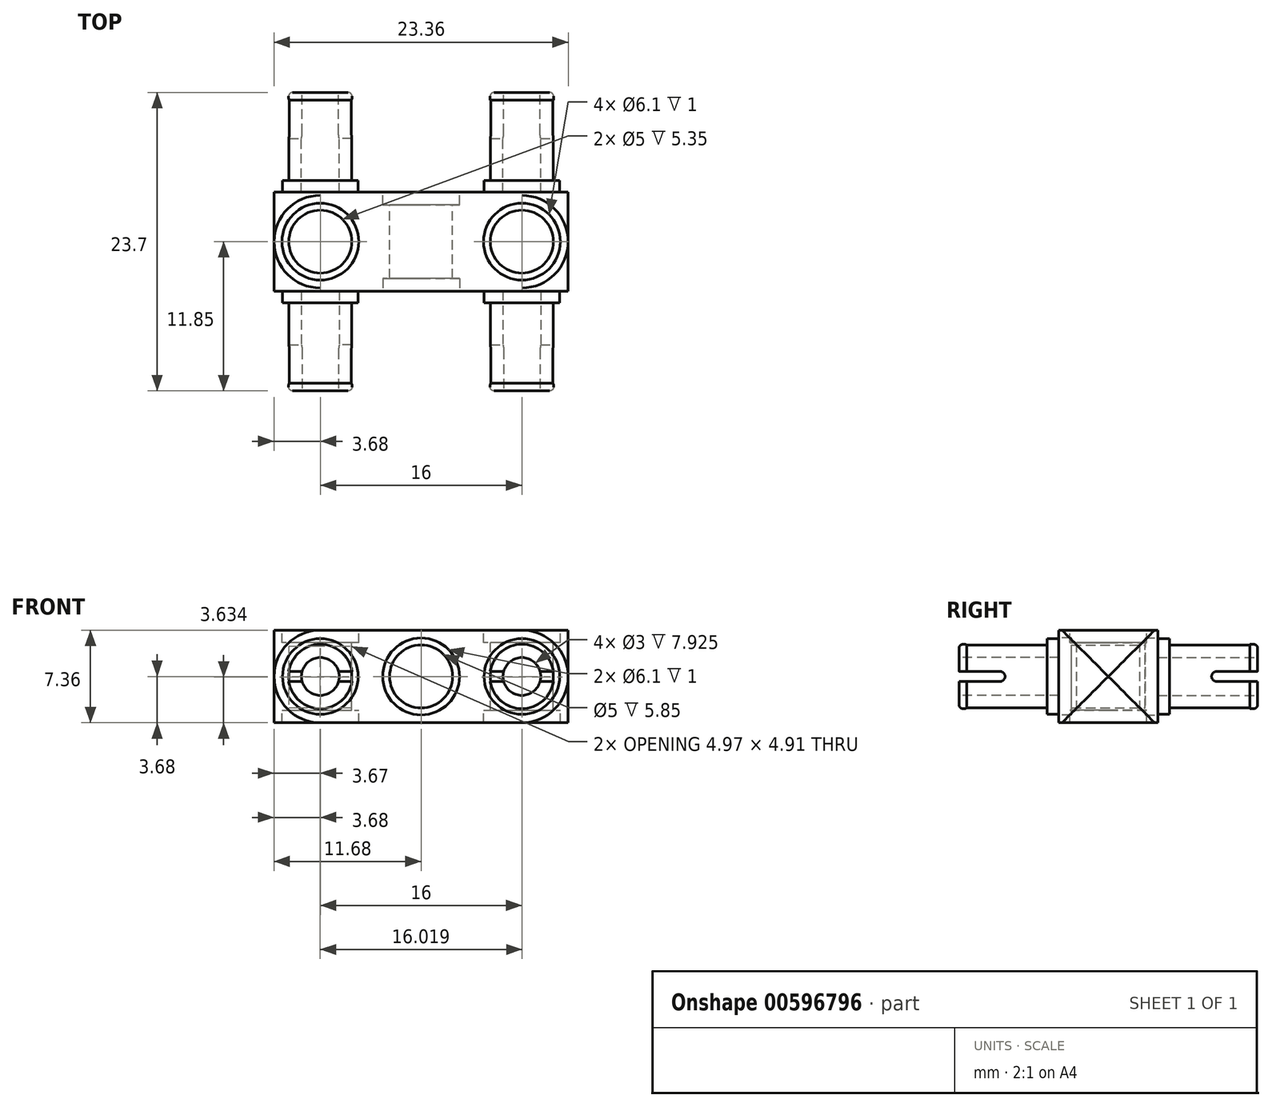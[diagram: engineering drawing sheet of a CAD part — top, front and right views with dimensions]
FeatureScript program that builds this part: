
annotation { "Feature Type Name" : "Feature", "Feature Type Description" : "" }
export const myFeature = defineFeature(function(context is Context, id is Id, definition is map)
    precondition{}
    {
        {
            var Q0;
            Q0=qCreatedBy(makeId("Front.planeOp"),FACE);
            var sketch = newSketch(context, id + "F0", { "sketchPlane" : qUnion([Q0])});
            skLineSegment(sketch, "E0.bottom", {"start": v(11.68, 3.67) * mm, "end": v(-11.68, 3.67) * mm});
            skLineSegment(sketch, "E0.top", {"start": v(11.68, -3.67) * mm, "end": v(-11.68, -3.67) * mm});
            skLineSegment(sketch, "E0.left", {"start": v(11.68, 3.67) * mm, "end": v(11.68, -3.67) * mm});
            skLineSegment(sketch, "E0.right", {"start": v(-11.68, 3.67) * mm, "end": v(-11.68, -3.67) * mm});
            skPoint(sketch, "E0.middle", {"position": v(0, 0) * mm});
            skCircle(sketch, "E1", {"center": v(-8, 0) * mm, "radius": 3.67 * mm});
            skCircle(sketch, "E2", {"center": v(8, 0) * mm, "radius": 3.67 * mm});
            skCircle(sketch, "E3", {"center": v(0, 0) * mm, "radius": 2.5 * mm});
            skCircle(sketch, "E4", {"center": v(0, 0) * mm, "radius": 3.05 * mm});
            skCircle(sketch, "E5", {"center": v(-8, 0) * mm, "radius": 3 * mm});
            skCircle(sketch, "E6", {"center": v(8, 0) * mm, "radius": 3 * mm});
            skCircle(sketch, "E7", {"center": v(-8, 0) * mm, "radius": 2.5 * mm});
            skCircle(sketch, "E8", {"center": v(8, 0) * mm, "radius": 2.5 * mm});
            skSolve(sketch);
        }
        {
            var Q0;
            Q0=makeQuery(id+"F0.imprint","IMPRINT",FACE,{"disambiguationData":[TD([[makeQuery(id+"F0.imprint","IMPRINT",EDGE,{"derivedFrom":sQuery(id+"F0.wireOp",EDGE,"E4")}),-1.0]])]});
            var Q1;
            {var subQ0=sQuery(id+"F0.wireOp",EDGE,"E1");var subQ1=makeQuery(id+"F0.imprint","INTERSECT",VERTEX,{"derivedFrom":[sQuery(id+"F0.wireOp",EDGE,"E0.bottom"),subQ0]});Q1=makeQuery(id+"F0.imprint","IMPRINT",FACE,{"disambiguationData":[TD([[makeQuery(id+"F0.imprint","IMPRINT",EDGE,{"disambiguationData":[TD([[subQ1,-1.0]])],"derivedFrom":subQ0}),1.0]])]});}
            var Q2;
            {var subQ0=sQuery(id+"F0.wireOp",EDGE,"E2");var subQ1=makeQuery(id+"F0.imprint","INTERSECT",VERTEX,{"derivedFrom":[sQuery(id+"F0.wireOp",EDGE,"E0.bottom"),subQ0]});Q2=makeQuery(id+"F0.imprint","IMPRINT",FACE,{"disambiguationData":[TD([[makeQuery(id+"F0.imprint","IMPRINT",EDGE,{"disambiguationData":[TD([[subQ1,1.0]])],"derivedFrom":subQ0}),1.0]])]});}
            var Q3;
            Q3=makeQuery(id+"F0.imprint","IMPRINT",FACE,{"disambiguationData":[TD([[makeQuery(id+"F0.imprint","IMPRINT",EDGE,{"derivedFrom":sQuery(id+"F0.wireOp",EDGE,"E3")}),-1.0]])]});
            extrude(context, id + "F1", {"entities" : qUnion([Q0, Q1, Q2, Q3]), "endBound" : BoundingType.SYMMETRIC, "depth" : 7.85 * mm, "offsetDistance" : 25 * mm});
        }
        {
            var Q0;
            Q0=makeQuery(id+"F0.imprint","IMPRINT",FACE,{"disambiguationData":[TD([[makeQuery(id+"F0.imprint","IMPRINT",EDGE,{"derivedFrom":sQuery(id+"F0.wireOp",EDGE,"E5")}),1.0]])]});
            var Q1;
            Q1=makeQuery(id+"F0.imprint","IMPRINT",FACE,{"disambiguationData":[TD([[makeQuery(id+"F0.imprint","IMPRINT",EDGE,{"derivedFrom":sQuery(id+"F0.wireOp",EDGE,"E6")}),1.0]])]});
            extrude(context, id + "F2", {"entities" : qUnion([Q0, Q1]), "operationType" : NewBodyOperationType.ADD, "endBound" : BoundingType.SYMMETRIC, "depth" : 9.7 * mm, "offsetDistance" : 25 * mm});
        }
        {
            var Q0;
            Q0=makeQuery(id+"F0.imprint","IMPRINT",FACE,{"disambiguationData":[TD([[makeQuery(id+"F0.imprint","IMPRINT",EDGE,{"derivedFrom":sQuery(id+"F0.wireOp",EDGE,"E7")}),1.0]])]});
            var Q1;
            Q1=makeQuery(id+"F0.imprint","IMPRINT",FACE,{"disambiguationData":[TD([[makeQuery(id+"F0.imprint","IMPRINT",EDGE,{"derivedFrom":sQuery(id+"F0.wireOp",EDGE,"E8")}),1.0]])]});
            extrude(context, id + "F3", {"entities" : qUnion([Q0, Q1]), "operationType" : NewBodyOperationType.ADD, "endBound" : BoundingType.SYMMETRIC, "depth" : 22.5 * mm, "offsetDistance" : 25 * mm});
        }
        {
            var Q0;
            Q0=makeQuery(id+"F3.opExtrude","CAP_FACE",FACE,{"disambiguationData":[OSD([sQuery(id+"F0.wireOp",EDGE,"E7")])],"isStart":false});
            var sketch = newSketch(context, id + "F4", { "sketchPlane" : qUnion([Q0])});
            skCircle(sketch, "E9", {"center": v(-8, 0) * mm, "radius": 2.55 * mm});
            skSolve(sketch);
        }
        {
            var Q0;
            Q0=qSketchRegion(id+"F4",true);
            extrude(context, id + "F5", {"entities" : qUnion([Q0]), "operationType" : NewBodyOperationType.ADD, "depth" : 0.6 * mm, "offsetDistance" : 25 * mm});
        }
        {
            var Q0;
            Q0=makeQuery(id+"F3.opExtrude","CAP_FACE",FACE,{"disambiguationData":[OSD([sQuery(id+"F0.wireOp",EDGE,"E8")])],"isStart":false});
            var sketch = newSketch(context, id + "F6", { "sketchPlane" : qUnion([Q0])});
            skCircle(sketch, "E10", {"center": v(8, 0) * mm, "radius": 2.55 * mm});
            skSolve(sketch);
        }
        {
            var Q0;
            Q0=qSketchRegion(id+"F6",true);
            extrude(context, id + "F7", {"entities" : qUnion([Q0]), "operationType" : NewBodyOperationType.ADD, "depth" : 0.6 * mm, "offsetDistance" : 25 * mm});
        }
        {
            var Q0;
            Q0=makeQuery(id+"F3.opExtrude","CAP_FACE",FACE,{"disambiguationData":[OSD([sQuery(id+"F0.wireOp",EDGE,"E7")])],"isStart":true});
            var sketch = newSketch(context, id + "F8", { "sketchPlane" : qUnion([Q0])});
            skCircle(sketch, "E11", {"center": v(8, 0) * mm, "radius": 2.55 * mm});
            skSolve(sketch);
        }
        {
            var Q0;
            Q0=qSketchRegion(id+"F8",true);
            extrude(context, id + "F9", {"entities" : qUnion([Q0]), "operationType" : NewBodyOperationType.ADD, "depth" : 0.6 * mm, "offsetDistance" : 25 * mm});
        }
        {
            var Q0;
            Q0=makeQuery(id+"F3.opExtrude","CAP_FACE",FACE,{"disambiguationData":[OSD([sQuery(id+"F0.wireOp",EDGE,"E8")])],"isStart":true});
            var sketch = newSketch(context, id + "F10", { "sketchPlane" : qUnion([Q0])});
            skCircle(sketch, "E12", {"center": v(-8, 0) * mm, "radius": 2.55 * mm});
            skSolve(sketch);
        }
        {
            var Q0;
            Q0=qSketchRegion(id+"F10",true);
            extrude(context, id + "F11", {"entities" : qUnion([Q0]), "operationType" : NewBodyOperationType.ADD, "depth" : 0.6 * mm, "offsetDistance" : 25 * mm});
        }
        {
            var Q0;
            Q0=makeQuery(id+"F9.opExtrude","CAP_FACE",FACE,{"disambiguationData":[OSD([sQuery(id+"F8.wireOp",EDGE,"E11")])],"isStart":false});
            var sketch = newSketch(context, id + "F12", { "sketchPlane" : qUnion([Q0])});
            skCircle(sketch, "E13", {"center": v(8, 0) * mm, "radius": 1.5 * mm});
            skSolve(sketch);
        }
        {
            var Q0;
            Q0=qSketchRegion(id+"F12",true);
            var Q1;
            Q1=makeQuery(id+"F1.opExtrude","CAP_FACE",FACE,{"disambiguationData":[OSD([sQuery(id+"F0.wireOp",EDGE,"E0.bottom"),sQuery(id+"F0.wireOp",EDGE,"E0.top"),sQuery(id+"F0.wireOp",EDGE,"E1"),sQuery(id+"F0.wireOp",EDGE,"E2"),sQuery(id+"F0.wireOp",EDGE,"E3"),sQuery(id+"F0.wireOp",EDGE,"E5"),sQuery(id+"F0.wireOp",EDGE,"E6")])],"isStart":true});
            extrude(context, id + "F13", {"entities" : qUnion([Q0]), "operationType" : NewBodyOperationType.REMOVE, "endBound" : BoundingType.UP_TO_SURFACE, "oppositeDirection" : true, "depth" : 25 * mm, "endBoundEntityFace" : qUnion([Q1]), "offsetDistance" : 25 * mm});
        }
        {
            var Q0;
            Q0=makeQuery(id+"F11.opExtrude","CAP_FACE",FACE,{"disambiguationData":[OSD([sQuery(id+"F10.wireOp",EDGE,"E12")])],"isStart":false});
            var sketch = newSketch(context, id + "F14", { "sketchPlane" : qUnion([Q0])});
            skCircle(sketch, "E14", {"center": v(-8, 0) * mm, "radius": 1.5 * mm});
            skSolve(sketch);
        }
        {
            var Q0;
            Q0=qSketchRegion(id+"F14",true);
            var Q1;
            Q1=makeQuery(id+"F1.opExtrude","CAP_FACE",FACE,{"disambiguationData":[OSD([sQuery(id+"F0.wireOp",EDGE,"E0.bottom"),sQuery(id+"F0.wireOp",EDGE,"E0.top"),sQuery(id+"F0.wireOp",EDGE,"E1"),sQuery(id+"F0.wireOp",EDGE,"E2"),sQuery(id+"F0.wireOp",EDGE,"E3"),sQuery(id+"F0.wireOp",EDGE,"E5"),sQuery(id+"F0.wireOp",EDGE,"E6")])],"isStart":true});
            extrude(context, id + "F15", {"entities" : qUnion([Q0]), "operationType" : NewBodyOperationType.REMOVE, "endBound" : BoundingType.UP_TO_SURFACE, "oppositeDirection" : true, "depth" : 25 * mm, "endBoundEntityFace" : qUnion([Q1]), "offsetDistance" : 25 * mm});
        }
        {
            var Q0;
            Q0=makeQuery(id+"F7.opExtrude","CAP_FACE",FACE,{"disambiguationData":[OSD([sQuery(id+"F6.wireOp",EDGE,"E10")])],"isStart":false});
            var sketch = newSketch(context, id + "F16", { "sketchPlane" : qUnion([Q0])});
            skCircle(sketch, "E15", {"center": v(8, 0) * mm, "radius": 1.5 * mm});
            skSolve(sketch);
        }
        {
            var Q0;
            Q0=qSketchRegion(id+"F16",true);
            var Q1;
            Q1=makeQuery(id+"F1.opExtrude","CAP_FACE",FACE,{"disambiguationData":[OSD([sQuery(id+"F0.wireOp",EDGE,"E0.bottom"),sQuery(id+"F0.wireOp",EDGE,"E0.top"),sQuery(id+"F0.wireOp",EDGE,"E1"),sQuery(id+"F0.wireOp",EDGE,"E2"),sQuery(id+"F0.wireOp",EDGE,"E3"),sQuery(id+"F0.wireOp",EDGE,"E5"),sQuery(id+"F0.wireOp",EDGE,"E6")])],"isStart":false});
            extrude(context, id + "F17", {"entities" : qUnion([Q0]), "operationType" : NewBodyOperationType.REMOVE, "endBound" : BoundingType.UP_TO_SURFACE, "oppositeDirection" : true, "depth" : 25 * mm, "endBoundEntityFace" : qUnion([Q1]), "offsetDistance" : 25 * mm});
        }
        {
            var Q0;
            Q0=makeQuery(id+"F5.opExtrude","CAP_FACE",FACE,{"disambiguationData":[OSD([sQuery(id+"F4.wireOp",EDGE,"E9")])],"isStart":false});
            var sketch = newSketch(context, id + "F18", { "sketchPlane" : qUnion([Q0])});
            skCircle(sketch, "E16", {"center": v(-8, 0) * mm, "radius": 1.5 * mm});
            skSolve(sketch);
        }
        {
            var Q0;
            Q0=qSketchRegion(id+"F18",true);
            var Q1;
            Q1=makeQuery(id+"F1.opExtrude","CAP_FACE",FACE,{"disambiguationData":[OSD([sQuery(id+"F0.wireOp",EDGE,"E0.bottom"),sQuery(id+"F0.wireOp",EDGE,"E0.top"),sQuery(id+"F0.wireOp",EDGE,"E1"),sQuery(id+"F0.wireOp",EDGE,"E2"),sQuery(id+"F0.wireOp",EDGE,"E3"),sQuery(id+"F0.wireOp",EDGE,"E5"),sQuery(id+"F0.wireOp",EDGE,"E6")])],"isStart":false});
            extrude(context, id + "F19", {"entities" : qUnion([Q0]), "operationType" : NewBodyOperationType.REMOVE, "endBound" : BoundingType.UP_TO_SURFACE, "oppositeDirection" : true, "depth" : 25 * mm, "endBoundEntityFace" : qUnion([Q1]), "offsetDistance" : 25 * mm});
        }
        {
            var Q0;
            Q0=makeQuery(id+"F5.opExtrude","CAP_EDGE",EDGE,{"disambiguationData":[OSD([sQuery(id+"F4.wireOp",EDGE,"E9")])],"isStart":false});
            var Q1;
            Q1=makeQuery(id+"F5.opExtrude","CAP_EDGE",EDGE,{"disambiguationData":[OSD([sQuery(id+"F4.wireOp",EDGE,"E9")])],"isStart":true});
            var Q2;
            Q2=makeQuery(id+"F7.opExtrude","CAP_EDGE",EDGE,{"disambiguationData":[OSD([sQuery(id+"F6.wireOp",EDGE,"E10")])],"isStart":false});
            var Q3;
            Q3=makeQuery(id+"F7.opExtrude","CAP_EDGE",EDGE,{"disambiguationData":[OSD([sQuery(id+"F6.wireOp",EDGE,"E10")])],"isStart":true});
            var Q4;
            Q4=makeQuery(id+"F9.opExtrude","CAP_EDGE",EDGE,{"disambiguationData":[OSD([sQuery(id+"F8.wireOp",EDGE,"E11")])],"isStart":false});
            var Q5;
            Q5=makeQuery(id+"F9.opExtrude","CAP_EDGE",EDGE,{"disambiguationData":[OSD([sQuery(id+"F8.wireOp",EDGE,"E11")])],"isStart":true});
            var Q6;
            Q6=makeQuery(id+"F11.opExtrude","CAP_EDGE",EDGE,{"disambiguationData":[OSD([sQuery(id+"F10.wireOp",EDGE,"E12")])],"isStart":false});
            var Q7;
            Q7=makeQuery(id+"F3.opExtrude","CAP_EDGE",EDGE,{"disambiguationData":[OSD([sQuery(id+"F0.wireOp",EDGE,"E8")])],"isStart":true});
            fillet(context, id + "F20", {"entities" : qUnion([Q0, Q1, Q2, Q3, Q4, Q5, Q6, Q7]), "radius" : 0.3 * mm, "tangentPropagation" : true, "allowEdgeOverflow" : false});
        }
        {
            var Q0;
            Q0=makeQuery(id+"F1.opExtrude","SWEPT_FACE",FACE,{"disambiguationData":[OSD([sQuery(id+"F0.wireOp",EDGE,"E0.bottom")])]});
            var sketch = newSketch(context, id + "F21", { "sketchPlane" : qUnion([Q0])});
            skCircle(sketch, "E17", {"center": v(-8, 0) * mm, "radius": 3.67 * mm});
            skCircle(sketch, "E18", {"center": v(8, 0) * mm, "radius": 3.67 * mm});
            skCircle(sketch, "E19", {"center": v(-8, 0) * mm, "radius": 2.5 * mm});
            skCircle(sketch, "E20", {"center": v(8, 0) * mm, "radius": 2.5 * mm});
            skCircle(sketch, "E21", {"center": v(-8, 0) * mm, "radius": 3.05 * mm});
            skCircle(sketch, "E22", {"center": v(8, 0) * mm, "radius": 3.05 * mm});
            skSolve(sketch);
        }
        {
            var Q0;
            Q0=qSketchRegion(id+"F21",true);
            var Q1;
            Q1=makeQuery(id+"F1.opExtrude","SWEPT_FACE",FACE,{"disambiguationData":[OSD([sQuery(id+"F0.wireOp",EDGE,"E0.top")])]});
            extrude(context, id + "F22", {"entities" : qUnion([Q0]), "operationType" : NewBodyOperationType.ADD, "endBound" : BoundingType.UP_TO_SURFACE, "oppositeDirection" : true, "depth" : 25 * mm, "endBoundEntityFace" : qUnion([Q1]), "offsetDistance" : 25 * mm});
        }
        {
            var Q0;
            {var subQ0=sQuery(id+"F21.wireOp",EDGE,"E19");var subQ1=makeQuery(id+"F1.opExtrude","SWEPT_EDGE",EDGE,{"disambiguationData":[OSD([sQuery(id+"F0.wireOp",EDGE,"E0.bottom"),sQuery(id+"F0.wireOp",EDGE,"E1")])]});var subQ2=makeQuery(id+"F21.imprint","INTERSECT",VERTEX,{"disambiguationData":[OD(0.0)],"derivedFrom":[subQ1,subQ0]});Q0=makeQuery(id+"F21.imprint","IMPRINT",FACE,{"disambiguationData":[TD([[makeQuery(id+"F21.imprint","IMPRINT",EDGE,{"disambiguationData":[TD([[subQ2,-1.0]])],"derivedFrom":subQ0}),1.0]])]});}
            var Q1;
            {var subQ0=sQuery(id+"F21.wireOp",EDGE,"E19");var subQ1=makeQuery(id+"F1.opExtrude","SWEPT_EDGE",EDGE,{"disambiguationData":[OSD([sQuery(id+"F0.wireOp",EDGE,"E0.bottom"),sQuery(id+"F0.wireOp",EDGE,"E1")])]});var subQ2=makeQuery(id+"F21.imprint","INTERSECT",VERTEX,{"disambiguationData":[OD(0.0)],"derivedFrom":[subQ1,subQ0]});Q1=makeQuery(id+"F21.imprint","IMPRINT",FACE,{"disambiguationData":[TD([[makeQuery(id+"F21.imprint","IMPRINT",EDGE,{"disambiguationData":[TD([[subQ2,1.0]])],"derivedFrom":subQ0}),1.0]])]});}
            var Q2;
            {var subQ0=sQuery(id+"F21.wireOp",EDGE,"E20");var subQ1=makeQuery(id+"F1.opExtrude","SWEPT_EDGE",EDGE,{"disambiguationData":[OSD([sQuery(id+"F0.wireOp",EDGE,"E0.bottom"),sQuery(id+"F0.wireOp",EDGE,"E2")])]});var subQ2=makeQuery(id+"F21.imprint","INTERSECT",VERTEX,{"disambiguationData":[OD(0.0)],"derivedFrom":[subQ1,subQ0]});Q2=makeQuery(id+"F21.imprint","IMPRINT",FACE,{"disambiguationData":[TD([[makeQuery(id+"F21.imprint","IMPRINT",EDGE,{"disambiguationData":[TD([[subQ2,-1.0]])],"derivedFrom":subQ0}),1.0]])]});}
            var Q3;
            {var subQ0=sQuery(id+"F21.wireOp",EDGE,"E20");var subQ1=makeQuery(id+"F1.opExtrude","SWEPT_EDGE",EDGE,{"disambiguationData":[OSD([sQuery(id+"F0.wireOp",EDGE,"E0.bottom"),sQuery(id+"F0.wireOp",EDGE,"E2")])]});var subQ2=makeQuery(id+"F21.imprint","INTERSECT",VERTEX,{"disambiguationData":[OD(0.0)],"derivedFrom":[subQ1,subQ0]});Q3=makeQuery(id+"F21.imprint","IMPRINT",FACE,{"disambiguationData":[TD([[makeQuery(id+"F21.imprint","IMPRINT",EDGE,{"disambiguationData":[TD([[subQ2,1.0]])],"derivedFrom":subQ0}),1.0]])]});}
            extrude(context, id + "F23", {"entities" : qUnion([Q0, Q1, Q2, Q3]), "operationType" : NewBodyOperationType.REMOVE, "endBound" : BoundingType.THROUGH_ALL, "oppositeDirection" : true, "depth" : 25 * mm, "offsetDistance" : 25 * mm});
        }
        {
            var Q0;
            {var subQ0=sQuery(id+"F21.wireOp",EDGE,"E19");var subQ1=makeQuery(id+"F1.opExtrude","SWEPT_EDGE",EDGE,{"disambiguationData":[OSD([sQuery(id+"F0.wireOp",EDGE,"E0.bottom"),sQuery(id+"F0.wireOp",EDGE,"E1")])]});var subQ2=makeQuery(id+"F21.imprint","INTERSECT",VERTEX,{"disambiguationData":[OD(0.0)],"derivedFrom":[subQ1,subQ0]});Q0=makeQuery(id+"F21.imprint","IMPRINT",FACE,{"disambiguationData":[TD([[makeQuery(id+"F21.imprint","IMPRINT",EDGE,{"disambiguationData":[TD([[subQ2,1.0]])],"derivedFrom":subQ0}),-1.0]])]});}
            var Q1;
            {var subQ0=sQuery(id+"F21.wireOp",EDGE,"E20");var subQ1=makeQuery(id+"F1.opExtrude","SWEPT_EDGE",EDGE,{"disambiguationData":[OSD([sQuery(id+"F0.wireOp",EDGE,"E0.bottom"),sQuery(id+"F0.wireOp",EDGE,"E2")])]});var subQ2=makeQuery(id+"F21.imprint","INTERSECT",VERTEX,{"disambiguationData":[OD(0.0)],"derivedFrom":[subQ1,subQ0]});Q1=makeQuery(id+"F21.imprint","IMPRINT",FACE,{"disambiguationData":[TD([[makeQuery(id+"F21.imprint","IMPRINT",EDGE,{"disambiguationData":[TD([[subQ2,-1.0]])],"derivedFrom":subQ0}),-1.0]])]});}
            var Q2;
            {var subQ0=sQuery(id+"F21.wireOp",EDGE,"E20");var subQ1=makeQuery(id+"F1.opExtrude","SWEPT_EDGE",EDGE,{"disambiguationData":[OSD([sQuery(id+"F0.wireOp",EDGE,"E0.bottom"),sQuery(id+"F0.wireOp",EDGE,"E2")])]});var subQ2=makeQuery(id+"F21.imprint","INTERSECT",VERTEX,{"disambiguationData":[OD(0.0)],"derivedFrom":[subQ1,subQ0]});Q2=makeQuery(id+"F21.imprint","IMPRINT",FACE,{"disambiguationData":[TD([[makeQuery(id+"F21.imprint","IMPRINT",EDGE,{"disambiguationData":[TD([[subQ2,1.0]])],"derivedFrom":subQ0}),-1.0]])]});}
            var Q3;
            {var subQ0=sQuery(id+"F21.wireOp",EDGE,"E19");var subQ1=makeQuery(id+"F1.opExtrude","SWEPT_EDGE",EDGE,{"disambiguationData":[OSD([sQuery(id+"F0.wireOp",EDGE,"E0.bottom"),sQuery(id+"F0.wireOp",EDGE,"E1")])]});var subQ2=makeQuery(id+"F21.imprint","INTERSECT",VERTEX,{"disambiguationData":[OD(0.0)],"derivedFrom":[subQ1,subQ0]});Q3=makeQuery(id+"F21.imprint","IMPRINT",FACE,{"disambiguationData":[TD([[makeQuery(id+"F21.imprint","IMPRINT",EDGE,{"disambiguationData":[TD([[subQ2,-1.0]])],"derivedFrom":subQ0}),-1.0]])]});}
            extrude(context, id + "F24", {"entities" : qUnion([Q0, Q1, Q2, Q3]), "operationType" : NewBodyOperationType.REMOVE, "oppositeDirection" : true, "depth" : 1 * mm, "offsetDistance" : 25 * mm});
        }
        {
            var Q0;
            Q0=makeQuery(id+"F22.boolean.opBoolean","MERGE",FACE,{"derivedFrom":[makeQuery(id+"F1.opExtrude","SWEPT_FACE",FACE,{"disambiguationData":[OSD([sQuery(id+"F0.wireOp",EDGE,"E0.top")])]}),makeQuery(id+"F22.opExtrude","CAP_FACE",FACE,{"disambiguationData":[OSD([sQuery(id+"F21.wireOp",EDGE,"E17"),sQuery(id+"F21.wireOp",EDGE,"E21")])],"isStart":false}),makeQuery(id+"F22.opExtrude","CAP_FACE",FACE,{"disambiguationData":[OSD([sQuery(id+"F21.wireOp",EDGE,"E18"),sQuery(id+"F21.wireOp",EDGE,"E22")])],"isStart":false})]});
            var sketch = newSketch(context, id + "F25", { "sketchPlane" : qUnion([Q0])});
            skCircle(sketch, "E23", {"center": v(-8, 0) * mm, "radius": 3.05 * mm});
            skCircle(sketch, "E24", {"center": v(-8, 0) * mm, "radius": 2.5 * mm});
            skCircle(sketch, "E25", {"center": v(8, 0) * mm, "radius": 2.5 * mm});
            skCircle(sketch, "E26", {"center": v(8, 0) * mm, "radius": 3.05 * mm});
            skSolve(sketch);
        }
        {
            var Q0;
            Q0=makeQuery(id+"F25.imprint","IMPRINT",FACE,{"disambiguationData":[TD([[makeQuery(id+"F25.imprint","IMPRINT",EDGE,{"disambiguationData":[OD(0.0)],"derivedFrom":sQuery(id+"F25.wireOp",EDGE,"E26")}),1.0]])]});
            var Q1;
            Q1=makeQuery(id+"F25.imprint","IMPRINT",FACE,{"disambiguationData":[TD([[makeQuery(id+"F25.imprint","IMPRINT",EDGE,{"disambiguationData":[OD(1.0)],"derivedFrom":sQuery(id+"F25.wireOp",EDGE,"E26")}),-1.0]])]});
            var Q2;
            Q2=makeQuery(id+"F25.imprint","IMPRINT",FACE,{"disambiguationData":[TD([[makeQuery(id+"F25.imprint","IMPRINT",EDGE,{"disambiguationData":[OD(1.0)],"derivedFrom":sQuery(id+"F25.wireOp",EDGE,"E23")}),-1.0]])]});
            var Q3;
            Q3=makeQuery(id+"F25.imprint","IMPRINT",FACE,{"disambiguationData":[TD([[makeQuery(id+"F25.imprint","IMPRINT",EDGE,{"disambiguationData":[OD(0.0)],"derivedFrom":sQuery(id+"F25.wireOp",EDGE,"E23")}),1.0]])]});
            extrude(context, id + "F26", {"entities" : qUnion([Q0, Q1, Q2, Q3]), "operationType" : NewBodyOperationType.REMOVE, "oppositeDirection" : true, "depth" : 1 * mm, "offsetDistance" : 25 * mm});
        }
        {
            var Q0;
            Q0=makeQuery(id+"F1.opExtrude","CAP_FACE",FACE,{"disambiguationData":[OSD([sQuery(id+"F0.wireOp",EDGE,"E0.bottom"),sQuery(id+"F0.wireOp",EDGE,"E0.top"),sQuery(id+"F0.wireOp",EDGE,"E1"),sQuery(id+"F0.wireOp",EDGE,"E2"),sQuery(id+"F0.wireOp",EDGE,"E3"),sQuery(id+"F0.wireOp",EDGE,"E5"),sQuery(id+"F0.wireOp",EDGE,"E6")])],"isStart":true});
            var sketch = newSketch(context, id + "F27", { "sketchPlane" : qUnion([Q0])});
            skCircle(sketch, "E27", {"center": v(0, 0) * mm, "radius": 3.05 * mm});
            skSolve(sketch);
        }
        {
            var Q0;
            Q0=makeQuery(id+"F27.imprint","IMPRINT",FACE,{"disambiguationData":[TD([[makeQuery(id+"F27.imprint","IMPRINT",EDGE,{"derivedFrom":sQuery(id+"F27.wireOp",EDGE,"E27")}),1.0]])]});
            extrude(context, id + "F28", {"entities" : qUnion([Q0]), "operationType" : NewBodyOperationType.REMOVE, "oppositeDirection" : true, "depth" : 1 * mm, "offsetDistance" : 25 * mm});
        }
        {
            var Q0;
            Q0=makeQuery(id+"F1.opExtrude","CAP_FACE",FACE,{"disambiguationData":[OSD([sQuery(id+"F0.wireOp",EDGE,"E0.bottom"),sQuery(id+"F0.wireOp",EDGE,"E0.top"),sQuery(id+"F0.wireOp",EDGE,"E1"),sQuery(id+"F0.wireOp",EDGE,"E2"),sQuery(id+"F0.wireOp",EDGE,"E3"),sQuery(id+"F0.wireOp",EDGE,"E5"),sQuery(id+"F0.wireOp",EDGE,"E6")])],"isStart":false});
            var sketch = newSketch(context, id + "F29", { "sketchPlane" : qUnion([Q0])});
            skCircle(sketch, "E28", {"center": v(0, 0) * mm, "radius": 3.05 * mm});
            skSolve(sketch);
        }
        {
            var Q0;
            Q0=makeQuery(id+"F29.imprint","IMPRINT",FACE,{"disambiguationData":[TD([[makeQuery(id+"F29.imprint","IMPRINT",EDGE,{"derivedFrom":sQuery(id+"F29.wireOp",EDGE,"E28")}),1.0]])]});
            extrude(context, id + "F30", {"entities" : qUnion([Q0]), "operationType" : NewBodyOperationType.REMOVE, "oppositeDirection" : true, "depth" : 1 * mm, "offsetDistance" : 25 * mm});
        }
        {
            var Q0;
            Q0=makeQuery(id+"F24.boolean.opBoolean","COPY",FACE,{"derivedFrom":makeQuery(id+"F24.opExtrude","CAP_FACE",FACE,{"disambiguationData":[OSD([sQuery(id+"F21.wireOp",EDGE,"E20"),sQuery(id+"F21.wireOp",EDGE,"E22")])],"isStart":false})});
            var sketch = newSketch(context, id + "F31", { "sketchPlane" : qUnion([Q0])});
            skCircle(sketch, "E29", {"center": v(8, 0) * mm, "radius": 3.05 * mm});
            skCircle(sketch, "E30", {"center": v(8, 0) * mm, "radius": 2.5 * mm});
            skSolve(sketch);
        }
        {
            var Q0;
            Q0=makeQuery(id+"F31.imprint","IMPRINT",FACE,{"disambiguationData":[TD([[makeQuery(id+"F31.imprint","IMPRINT",EDGE,{"derivedFrom":sQuery(id+"F31.wireOp",EDGE,"E30")}),-1.0]])]});
            var Q1;
            {var subQ1=sQuery(id+"F21.wireOp",EDGE,"E22");var subQ2=makeQuery(id+"F24.boolean.opBoolean","INTERSECT",EDGE,{"derivedFrom":[makeQuery(id+"F22.boolean.opBoolean","SPLIT",FACE,{"disambiguationData":[TD([makeQuery(id+"F1.opExtrude","SWEPT_FACE",FACE,{"disambiguationData":[OSD([sQuery(id+"F0.wireOp",EDGE,"E0.bottom")])]}),makeQuery(id+"F22.opExtrude","CAP_FACE",FACE,{"disambiguationData":[OSD([sQuery(id+"F21.wireOp",EDGE,"E17"),sQuery(id+"F21.wireOp",EDGE,"E21")])],"isStart":true}),makeQuery(id+"F22.opExtrude","CAP_FACE",FACE,{"disambiguationData":[OSD([sQuery(id+"F21.wireOp",EDGE,"E18"),subQ1])],"isStart":true}),makeQuery(id+"F22.opExtrude","SWEPT_FACE",FACE,{"disambiguationData":[OSD([subQ1])]})])],"derivedFrom":makeQuery(id+"F1.opExtrude","SWEPT_FACE",FACE,{"disambiguationData":[OSD([sQuery(id+"F0.wireOp",EDGE,"E2")])]})}),makeQuery(id+"F24.opExtrude","CAP_FACE",FACE,{"disambiguationData":[OSD([sQuery(id+"F21.wireOp",EDGE,"E20"),subQ1])],"isStart":false})]});Q1=makeQuery(id+"F31.imprint","IMPRINT",FACE,{"disambiguationData":[TD([[makeQuery(id+"F31.imprint","IMPRINT",EDGE,{"derivedFrom":subQ2}),-1.0]])]});}
            var Q2;
            Q2=makeQuery(id+"F26.boolean.opBoolean","COPY",FACE,{"derivedFrom":makeQuery(id+"F26.opExtrude","CAP_FACE",FACE,{"disambiguationData":[OSD([sQuery(id+"F25.wireOp",EDGE,"E25"),sQuery(id+"F25.wireOp",EDGE,"E26")])],"isStart":false})});
            extrude(context, id + "F32", {"entities" : qUnion([Q0, Q1]), "operationType" : NewBodyOperationType.ADD, "endBound" : BoundingType.UP_TO_SURFACE, "oppositeDirection" : true, "depth" : 25 * mm, "endBoundEntityFace" : qUnion([Q2]), "offsetDistance" : 25 * mm});
        }
        {
            var Q0;
            Q0=makeQuery(id+"F24.boolean.opBoolean","COPY",FACE,{"derivedFrom":makeQuery(id+"F24.opExtrude","CAP_FACE",FACE,{"disambiguationData":[OSD([sQuery(id+"F21.wireOp",EDGE,"E19"),sQuery(id+"F21.wireOp",EDGE,"E21")])],"isStart":false})});
            var sketch = newSketch(context, id + "F33", { "sketchPlane" : qUnion([Q0])});
            skCircle(sketch, "E31", {"center": v(-8, 0) * mm, "radius": 3.05 * mm});
            skCircle(sketch, "E32", {"center": v(-8, 0) * mm, "radius": 2.5 * mm});
            skSolve(sketch);
        }
        {
            var Q0;
            Q0=makeQuery(id+"F33.imprint","IMPRINT",FACE,{"disambiguationData":[TD([[makeQuery(id+"F33.imprint","IMPRINT",EDGE,{"derivedFrom":sQuery(id+"F33.wireOp",EDGE,"E32")}),-1.0]])]});
            var Q1;
            {var subQ1=sQuery(id+"F21.wireOp",EDGE,"E21");var subQ2=makeQuery(id+"F24.boolean.opBoolean","INTERSECT",EDGE,{"derivedFrom":[makeQuery(id+"F22.boolean.opBoolean","SPLIT",FACE,{"disambiguationData":[TD([makeQuery(id+"F1.opExtrude","SWEPT_FACE",FACE,{"disambiguationData":[OSD([sQuery(id+"F0.wireOp",EDGE,"E0.bottom")])]}),makeQuery(id+"F22.opExtrude","CAP_FACE",FACE,{"disambiguationData":[OSD([sQuery(id+"F21.wireOp",EDGE,"E17"),subQ1])],"isStart":true}),makeQuery(id+"F22.opExtrude","CAP_FACE",FACE,{"disambiguationData":[OSD([sQuery(id+"F21.wireOp",EDGE,"E18"),sQuery(id+"F21.wireOp",EDGE,"E22")])],"isStart":true}),makeQuery(id+"F22.opExtrude","SWEPT_FACE",FACE,{"disambiguationData":[OSD([subQ1])]})])],"derivedFrom":makeQuery(id+"F1.opExtrude","SWEPT_FACE",FACE,{"disambiguationData":[OSD([sQuery(id+"F0.wireOp",EDGE,"E1")])]})}),makeQuery(id+"F24.opExtrude","CAP_FACE",FACE,{"disambiguationData":[OSD([sQuery(id+"F21.wireOp",EDGE,"E19"),subQ1])],"isStart":false})]});Q1=makeQuery(id+"F33.imprint","IMPRINT",FACE,{"disambiguationData":[TD([[makeQuery(id+"F33.imprint","IMPRINT",EDGE,{"derivedFrom":subQ2}),-1.0]])]});}
            var Q2;
            Q2=makeQuery(id+"F26.boolean.opBoolean","COPY",FACE,{"derivedFrom":makeQuery(id+"F26.opExtrude","CAP_FACE",FACE,{"disambiguationData":[OSD([sQuery(id+"F25.wireOp",EDGE,"E23"),sQuery(id+"F25.wireOp",EDGE,"E24")])],"isStart":false})});
            extrude(context, id + "F34", {"entities" : qUnion([Q0, Q1]), "operationType" : NewBodyOperationType.ADD, "endBound" : BoundingType.UP_TO_SURFACE, "oppositeDirection" : true, "depth" : 25 * mm, "endBoundEntityFace" : qUnion([Q2]), "offsetDistance" : 25 * mm});
        }
        {
            var Q0;
            Q0=qCreatedBy(makeId("Right.planeOp"),FACE);
            var sketch = newSketch(context, id + "F35", { "sketchPlane" : qUnion([Q0])});
            skLineSegment(sketch, "E33", {"start": v(0, 0) * mm, "end": v(8.2, 0) * mm, "construction": true});
            skLineSegment(sketch, "E34", {"start": v(0, 0) * mm, "end": v(-8.2, 0) * mm, "construction": true});
            skLineSegment(sketch, "E35.bottom", {"start": v(-8.2, 0.4) * mm, "end": v(-11.85, 0.4) * mm});
            skLineSegment(sketch, "E35.top", {"start": v(-8.2, -0.4) * mm, "end": v(-11.85, -0.4) * mm});
            skLineSegment(sketch, "E35.left", {"start": v(-8.2, 0.4) * mm, "end": v(-8.2, -0.4) * mm});
            skPoint(sketch, "E35.middle", {"position": v(-12.33, 0) * mm});
            skLineSegment(sketch, "E36.bottom", {"start": v(8.2, -0.4) * mm, "end": v(11.85, -0.4) * mm});
            skLineSegment(sketch, "E36.top", {"start": v(8.2, 0.4) * mm, "end": v(11.85, 0.4) * mm});
            skLineSegment(sketch, "E36.left", {"start": v(8.2, -0.4) * mm, "end": v(8.2, 0.4) * mm});
            skPoint(sketch, "E36.middle", {"position": v(15.2, 0) * mm});
            skPoint(sketch, "E36.middle.positionSnap0", {"position": v(-4.1, 0) * mm});
            skPoint(sketch, "E36.centerSnap0", {"position": v(-4.1, 0) * mm});
            skLineSegment(sketch, "E37", {"start": v(-11.85, 0.4) * mm, "end": v(-11.85, -0.4) * mm});
            skLineSegment(sketch, "E38", {"start": v(11.85, 0.4) * mm, "end": v(11.85, -0.4) * mm});
            skPoint(sketch, "E36.right.end.orphan", {"position": v(22.18, 0.4) * mm});
            skPoint(sketch, "E36.right.start.orphan", {"position": v(22.18, -0.4) * mm});
            skPoint(sketch, "E39.orphan", {"position": v(-16.46, 0.4) * mm});
            skPoint(sketch, "E40.orphan", {"position": v(-16.46, -0.4) * mm});
            skSolve(sketch);
        }
        {
            var Q0;
            Q0=makeQuery(id+"F35.imprint","IMPRINT",FACE,{"disambiguationData":[TD([[makeQuery(id+"F35.imprint","IMPRINT",EDGE,{"derivedFrom":sQuery(id+"F35.wireOp",EDGE,"E36.bottom")}),1.0]])]});
            var Q1;
            Q1=makeQuery(id+"F35.imprint","IMPRINT",FACE,{"disambiguationData":[TD([[makeQuery(id+"F35.imprint","IMPRINT",EDGE,{"derivedFrom":sQuery(id+"F35.wireOp",EDGE,"E35.bottom")}),1.0]])]});
            extrude(context, id + "F36", {"entities" : qUnion([Q0, Q1]), "operationType" : NewBodyOperationType.REMOVE, "endBound" : BoundingType.SYMMETRIC, "oppositeDirection" : true, "depth" : 25 * mm, "offsetDistance" : 25 * mm});
        }
        {
            var Q0;
            {var subQ0=sQuery(id+"F35.wireOp",EDGE,"E36.bottom");var subQ1=sQuery(id+"F35.wireOp",EDGE,"E36.left");Q0=makeQuery(id+"F36.boolean.opBoolean","COPY",EDGE,{"disambiguationData":[TD([makeQuery(id+"F3.opExtrude","SWEPT_FACE",FACE,{"disambiguationData":[OSD([sQuery(id+"F0.wireOp",EDGE,"E8")])]}),makeQuery(id+"F15.boolean.opBoolean","COPY",FACE,{"derivedFrom":makeQuery(id+"F15.opExtrude","SWEPT_FACE",FACE,{"disambiguationData":[OSD([sQuery(id+"F14.wireOp",EDGE,"E14")])]})}),makeQuery(id+"F36.opExtrude","SWEPT_FACE",FACE,{"disambiguationData":[OSD([subQ0])]}),makeQuery(id+"F36.opExtrude","SWEPT_FACE",FACE,{"disambiguationData":[OSD([subQ1])]})]),OD(1.0)],"derivedFrom":makeQuery(id+"F36.opExtrude","SWEPT_EDGE",EDGE,{"disambiguationData":[OSD([subQ0,subQ1])]})});}
            var Q1;
            {var subQ0=sQuery(id+"F35.wireOp",EDGE,"E36.top");var subQ1=sQuery(id+"F35.wireOp",EDGE,"E36.left");Q1=makeQuery(id+"F36.boolean.opBoolean","COPY",EDGE,{"disambiguationData":[TD([makeQuery(id+"F3.opExtrude","SWEPT_FACE",FACE,{"disambiguationData":[OSD([sQuery(id+"F0.wireOp",EDGE,"E8")])]}),makeQuery(id+"F15.boolean.opBoolean","COPY",FACE,{"derivedFrom":makeQuery(id+"F15.opExtrude","SWEPT_FACE",FACE,{"disambiguationData":[OSD([sQuery(id+"F14.wireOp",EDGE,"E14")])]})}),makeQuery(id+"F36.opExtrude","SWEPT_FACE",FACE,{"disambiguationData":[OSD([subQ0])]}),makeQuery(id+"F36.opExtrude","SWEPT_FACE",FACE,{"disambiguationData":[OSD([subQ1])]})]),OD(1.0)],"derivedFrom":makeQuery(id+"F36.opExtrude","SWEPT_EDGE",EDGE,{"disambiguationData":[OSD([subQ0,subQ1])]})});}
            var Q2;
            {var subQ0=sQuery(id+"F35.wireOp",EDGE,"E36.top");var subQ1=sQuery(id+"F35.wireOp",EDGE,"E36.left");Q2=makeQuery(id+"F36.boolean.opBoolean","COPY",EDGE,{"disambiguationData":[TD([makeQuery(id+"F3.opExtrude","SWEPT_FACE",FACE,{"disambiguationData":[OSD([sQuery(id+"F0.wireOp",EDGE,"E7")])]}),makeQuery(id+"F13.boolean.opBoolean","COPY",FACE,{"derivedFrom":makeQuery(id+"F13.opExtrude","SWEPT_FACE",FACE,{"disambiguationData":[OSD([sQuery(id+"F12.wireOp",EDGE,"E13")])]})}),makeQuery(id+"F36.opExtrude","SWEPT_FACE",FACE,{"disambiguationData":[OSD([subQ0])]}),makeQuery(id+"F36.opExtrude","SWEPT_FACE",FACE,{"disambiguationData":[OSD([subQ1])]})]),OD(1.0)],"derivedFrom":makeQuery(id+"F36.opExtrude","SWEPT_EDGE",EDGE,{"disambiguationData":[OSD([subQ0,subQ1])]})});}
            var Q3;
            {var subQ0=sQuery(id+"F35.wireOp",EDGE,"E35.left");var subQ1=sQuery(id+"F35.wireOp",EDGE,"E35.bottom");Q3=makeQuery(id+"F36.boolean.opBoolean","COPY",EDGE,{"disambiguationData":[TD([makeQuery(id+"F3.opExtrude","SWEPT_FACE",FACE,{"disambiguationData":[OSD([sQuery(id+"F0.wireOp",EDGE,"E8")])]}),makeQuery(id+"F17.boolean.opBoolean","COPY",FACE,{"derivedFrom":makeQuery(id+"F17.opExtrude","SWEPT_FACE",FACE,{"disambiguationData":[OSD([sQuery(id+"F16.wireOp",EDGE,"E15")])]})}),makeQuery(id+"F36.opExtrude","SWEPT_FACE",FACE,{"disambiguationData":[OSD([subQ1])]}),makeQuery(id+"F36.opExtrude","SWEPT_FACE",FACE,{"disambiguationData":[OSD([subQ0])]})]),OD(1.0)],"derivedFrom":makeQuery(id+"F36.opExtrude","SWEPT_EDGE",EDGE,{"disambiguationData":[OSD([subQ1,subQ0])]})});}
            var Q4;
            {var subQ0=sQuery(id+"F35.wireOp",EDGE,"E36.bottom");var subQ1=sQuery(id+"F35.wireOp",EDGE,"E36.left");Q4=makeQuery(id+"F36.boolean.opBoolean","COPY",EDGE,{"disambiguationData":[TD([makeQuery(id+"F3.opExtrude","SWEPT_FACE",FACE,{"disambiguationData":[OSD([sQuery(id+"F0.wireOp",EDGE,"E7")])]}),makeQuery(id+"F13.boolean.opBoolean","COPY",FACE,{"derivedFrom":makeQuery(id+"F13.opExtrude","SWEPT_FACE",FACE,{"disambiguationData":[OSD([sQuery(id+"F12.wireOp",EDGE,"E13")])]})}),makeQuery(id+"F36.opExtrude","SWEPT_FACE",FACE,{"disambiguationData":[OSD([subQ0])]}),makeQuery(id+"F36.opExtrude","SWEPT_FACE",FACE,{"disambiguationData":[OSD([subQ1])]})]),OD(1.0)],"derivedFrom":makeQuery(id+"F36.opExtrude","SWEPT_EDGE",EDGE,{"disambiguationData":[OSD([subQ0,subQ1])]})});}
            var Q5;
            {var subQ0=sQuery(id+"F35.wireOp",EDGE,"E35.top");var subQ1=sQuery(id+"F35.wireOp",EDGE,"E35.left");Q5=makeQuery(id+"F36.boolean.opBoolean","COPY",EDGE,{"disambiguationData":[TD([makeQuery(id+"F3.opExtrude","SWEPT_FACE",FACE,{"disambiguationData":[OSD([sQuery(id+"F0.wireOp",EDGE,"E8")])]}),makeQuery(id+"F17.boolean.opBoolean","COPY",FACE,{"derivedFrom":makeQuery(id+"F17.opExtrude","SWEPT_FACE",FACE,{"disambiguationData":[OSD([sQuery(id+"F16.wireOp",EDGE,"E15")])]})}),makeQuery(id+"F36.opExtrude","SWEPT_FACE",FACE,{"disambiguationData":[OSD([subQ0])]}),makeQuery(id+"F36.opExtrude","SWEPT_FACE",FACE,{"disambiguationData":[OSD([subQ1])]})]),OD(1.0)],"derivedFrom":makeQuery(id+"F36.opExtrude","SWEPT_EDGE",EDGE,{"disambiguationData":[OSD([subQ0,subQ1])]})});}
            var Q6;
            {var subQ0=sQuery(id+"F35.wireOp",EDGE,"E35.top");var subQ1=sQuery(id+"F35.wireOp",EDGE,"E35.left");Q6=makeQuery(id+"F36.boolean.opBoolean","COPY",EDGE,{"disambiguationData":[TD([makeQuery(id+"F3.opExtrude","SWEPT_FACE",FACE,{"disambiguationData":[OSD([sQuery(id+"F0.wireOp",EDGE,"E7")])]}),makeQuery(id+"F19.boolean.opBoolean","COPY",FACE,{"derivedFrom":makeQuery(id+"F19.opExtrude","SWEPT_FACE",FACE,{"disambiguationData":[OSD([sQuery(id+"F18.wireOp",EDGE,"E16")])]})}),makeQuery(id+"F36.opExtrude","SWEPT_FACE",FACE,{"disambiguationData":[OSD([subQ0])]}),makeQuery(id+"F36.opExtrude","SWEPT_FACE",FACE,{"disambiguationData":[OSD([subQ1])]})]),OD(1.0)],"derivedFrom":makeQuery(id+"F36.opExtrude","SWEPT_EDGE",EDGE,{"disambiguationData":[OSD([subQ0,subQ1])]})});}
            var Q7;
            {var subQ0=sQuery(id+"F35.wireOp",EDGE,"E35.bottom");var subQ1=sQuery(id+"F35.wireOp",EDGE,"E35.left");Q7=makeQuery(id+"F36.boolean.opBoolean","COPY",EDGE,{"disambiguationData":[TD([makeQuery(id+"F3.opExtrude","SWEPT_FACE",FACE,{"disambiguationData":[OSD([sQuery(id+"F0.wireOp",EDGE,"E7")])]}),makeQuery(id+"F19.boolean.opBoolean","COPY",FACE,{"derivedFrom":makeQuery(id+"F19.opExtrude","SWEPT_FACE",FACE,{"disambiguationData":[OSD([sQuery(id+"F18.wireOp",EDGE,"E16")])]})}),makeQuery(id+"F36.opExtrude","SWEPT_FACE",FACE,{"disambiguationData":[OSD([subQ0])]}),makeQuery(id+"F36.opExtrude","SWEPT_FACE",FACE,{"disambiguationData":[OSD([subQ1])]})]),OD(1.0)],"derivedFrom":makeQuery(id+"F36.opExtrude","SWEPT_EDGE",EDGE,{"disambiguationData":[OSD([subQ0,subQ1])]})});}
            var Q8;
            {var subQ0=sQuery(id+"F35.wireOp",EDGE,"E35.bottom");var subQ1=sQuery(id+"F35.wireOp",EDGE,"E35.left");Q8=makeQuery(id+"F36.boolean.opBoolean","COPY",EDGE,{"disambiguationData":[TD([makeQuery(id+"F3.opExtrude","SWEPT_FACE",FACE,{"disambiguationData":[OSD([sQuery(id+"F0.wireOp",EDGE,"E7")])]}),makeQuery(id+"F19.boolean.opBoolean","COPY",FACE,{"derivedFrom":makeQuery(id+"F19.opExtrude","SWEPT_FACE",FACE,{"disambiguationData":[OSD([sQuery(id+"F18.wireOp",EDGE,"E16")])]})}),makeQuery(id+"F36.opExtrude","SWEPT_FACE",FACE,{"disambiguationData":[OSD([subQ0])]}),makeQuery(id+"F36.opExtrude","SWEPT_FACE",FACE,{"disambiguationData":[OSD([subQ1])]})]),OD(0.0)],"derivedFrom":makeQuery(id+"F36.opExtrude","SWEPT_EDGE",EDGE,{"disambiguationData":[OSD([subQ0,subQ1])]})});}
            var Q9;
            {var subQ0=sQuery(id+"F35.wireOp",EDGE,"E35.top");var subQ1=sQuery(id+"F35.wireOp",EDGE,"E35.left");Q9=makeQuery(id+"F36.boolean.opBoolean","COPY",EDGE,{"disambiguationData":[TD([makeQuery(id+"F3.opExtrude","SWEPT_FACE",FACE,{"disambiguationData":[OSD([sQuery(id+"F0.wireOp",EDGE,"E7")])]}),makeQuery(id+"F19.boolean.opBoolean","COPY",FACE,{"derivedFrom":makeQuery(id+"F19.opExtrude","SWEPT_FACE",FACE,{"disambiguationData":[OSD([sQuery(id+"F18.wireOp",EDGE,"E16")])]})}),makeQuery(id+"F36.opExtrude","SWEPT_FACE",FACE,{"disambiguationData":[OSD([subQ0])]}),makeQuery(id+"F36.opExtrude","SWEPT_FACE",FACE,{"disambiguationData":[OSD([subQ1])]})]),OD(0.0)],"derivedFrom":makeQuery(id+"F36.opExtrude","SWEPT_EDGE",EDGE,{"disambiguationData":[OSD([subQ0,subQ1])]})});}
            var Q10;
            {var subQ0=sQuery(id+"F35.wireOp",EDGE,"E36.bottom");var subQ1=sQuery(id+"F35.wireOp",EDGE,"E36.left");Q10=makeQuery(id+"F36.boolean.opBoolean","COPY",EDGE,{"disambiguationData":[TD([makeQuery(id+"F3.opExtrude","SWEPT_FACE",FACE,{"disambiguationData":[OSD([sQuery(id+"F0.wireOp",EDGE,"E7")])]}),makeQuery(id+"F13.boolean.opBoolean","COPY",FACE,{"derivedFrom":makeQuery(id+"F13.opExtrude","SWEPT_FACE",FACE,{"disambiguationData":[OSD([sQuery(id+"F12.wireOp",EDGE,"E13")])]})}),makeQuery(id+"F36.opExtrude","SWEPT_FACE",FACE,{"disambiguationData":[OSD([subQ0])]}),makeQuery(id+"F36.opExtrude","SWEPT_FACE",FACE,{"disambiguationData":[OSD([subQ1])]})]),OD(0.0)],"derivedFrom":makeQuery(id+"F36.opExtrude","SWEPT_EDGE",EDGE,{"disambiguationData":[OSD([subQ0,subQ1])]})});}
            var Q11;
            {var subQ0=sQuery(id+"F35.wireOp",EDGE,"E36.bottom");var subQ1=sQuery(id+"F35.wireOp",EDGE,"E36.left");Q11=makeQuery(id+"F36.boolean.opBoolean","COPY",EDGE,{"disambiguationData":[TD([makeQuery(id+"F3.opExtrude","SWEPT_FACE",FACE,{"disambiguationData":[OSD([sQuery(id+"F0.wireOp",EDGE,"E8")])]}),makeQuery(id+"F15.boolean.opBoolean","COPY",FACE,{"derivedFrom":makeQuery(id+"F15.opExtrude","SWEPT_FACE",FACE,{"disambiguationData":[OSD([sQuery(id+"F14.wireOp",EDGE,"E14")])]})}),makeQuery(id+"F36.opExtrude","SWEPT_FACE",FACE,{"disambiguationData":[OSD([subQ0])]}),makeQuery(id+"F36.opExtrude","SWEPT_FACE",FACE,{"disambiguationData":[OSD([subQ1])]})]),OD(0.0)],"derivedFrom":makeQuery(id+"F36.opExtrude","SWEPT_EDGE",EDGE,{"disambiguationData":[OSD([subQ0,subQ1])]})});}
            var Q12;
            {var subQ0=sQuery(id+"F35.wireOp",EDGE,"E36.top");var subQ1=sQuery(id+"F35.wireOp",EDGE,"E36.left");Q12=makeQuery(id+"F36.boolean.opBoolean","COPY",EDGE,{"disambiguationData":[TD([makeQuery(id+"F3.opExtrude","SWEPT_FACE",FACE,{"disambiguationData":[OSD([sQuery(id+"F0.wireOp",EDGE,"E7")])]}),makeQuery(id+"F13.boolean.opBoolean","COPY",FACE,{"derivedFrom":makeQuery(id+"F13.opExtrude","SWEPT_FACE",FACE,{"disambiguationData":[OSD([sQuery(id+"F12.wireOp",EDGE,"E13")])]})}),makeQuery(id+"F36.opExtrude","SWEPT_FACE",FACE,{"disambiguationData":[OSD([subQ0])]}),makeQuery(id+"F36.opExtrude","SWEPT_FACE",FACE,{"disambiguationData":[OSD([subQ1])]})]),OD(0.0)],"derivedFrom":makeQuery(id+"F36.opExtrude","SWEPT_EDGE",EDGE,{"disambiguationData":[OSD([subQ0,subQ1])]})});}
            var Q13;
            {var subQ0=sQuery(id+"F35.wireOp",EDGE,"E36.top");var subQ1=sQuery(id+"F35.wireOp",EDGE,"E36.left");Q13=makeQuery(id+"F36.boolean.opBoolean","COPY",EDGE,{"disambiguationData":[TD([makeQuery(id+"F3.opExtrude","SWEPT_FACE",FACE,{"disambiguationData":[OSD([sQuery(id+"F0.wireOp",EDGE,"E8")])]}),makeQuery(id+"F15.boolean.opBoolean","COPY",FACE,{"derivedFrom":makeQuery(id+"F15.opExtrude","SWEPT_FACE",FACE,{"disambiguationData":[OSD([sQuery(id+"F14.wireOp",EDGE,"E14")])]})}),makeQuery(id+"F36.opExtrude","SWEPT_FACE",FACE,{"disambiguationData":[OSD([subQ0])]}),makeQuery(id+"F36.opExtrude","SWEPT_FACE",FACE,{"disambiguationData":[OSD([subQ1])]})]),OD(0.0)],"derivedFrom":makeQuery(id+"F36.opExtrude","SWEPT_EDGE",EDGE,{"disambiguationData":[OSD([subQ0,subQ1])]})});}
            var Q14;
            {var subQ0=sQuery(id+"F35.wireOp",EDGE,"E35.left");var subQ1=sQuery(id+"F35.wireOp",EDGE,"E35.bottom");Q14=makeQuery(id+"F36.boolean.opBoolean","COPY",EDGE,{"disambiguationData":[TD([makeQuery(id+"F3.opExtrude","SWEPT_FACE",FACE,{"disambiguationData":[OSD([sQuery(id+"F0.wireOp",EDGE,"E8")])]}),makeQuery(id+"F17.boolean.opBoolean","COPY",FACE,{"derivedFrom":makeQuery(id+"F17.opExtrude","SWEPT_FACE",FACE,{"disambiguationData":[OSD([sQuery(id+"F16.wireOp",EDGE,"E15")])]})}),makeQuery(id+"F36.opExtrude","SWEPT_FACE",FACE,{"disambiguationData":[OSD([subQ1])]}),makeQuery(id+"F36.opExtrude","SWEPT_FACE",FACE,{"disambiguationData":[OSD([subQ0])]})]),OD(0.0)],"derivedFrom":makeQuery(id+"F36.opExtrude","SWEPT_EDGE",EDGE,{"disambiguationData":[OSD([subQ1,subQ0])]})});}
            var Q15;
            {var subQ0=sQuery(id+"F35.wireOp",EDGE,"E35.top");var subQ1=sQuery(id+"F35.wireOp",EDGE,"E35.left");Q15=makeQuery(id+"F36.boolean.opBoolean","COPY",EDGE,{"disambiguationData":[TD([makeQuery(id+"F3.opExtrude","SWEPT_FACE",FACE,{"disambiguationData":[OSD([sQuery(id+"F0.wireOp",EDGE,"E8")])]}),makeQuery(id+"F17.boolean.opBoolean","COPY",FACE,{"derivedFrom":makeQuery(id+"F17.opExtrude","SWEPT_FACE",FACE,{"disambiguationData":[OSD([sQuery(id+"F16.wireOp",EDGE,"E15")])]})}),makeQuery(id+"F36.opExtrude","SWEPT_FACE",FACE,{"disambiguationData":[OSD([subQ0])]}),makeQuery(id+"F36.opExtrude","SWEPT_FACE",FACE,{"disambiguationData":[OSD([subQ1])]})]),OD(0.0)],"derivedFrom":makeQuery(id+"F36.opExtrude","SWEPT_EDGE",EDGE,{"disambiguationData":[OSD([subQ0,subQ1])]})});}
            fillet(context, id + "F37", {"entities" : qUnion([Q0, Q1, Q2, Q3, Q4, Q5, Q6, Q7, Q8, Q9, Q10, Q11, Q12, Q13, Q14, Q15]), "radius" : 0.4 * mm, "tangentPropagation" : true, "allowEdgeOverflow" : false});
        }
    });
